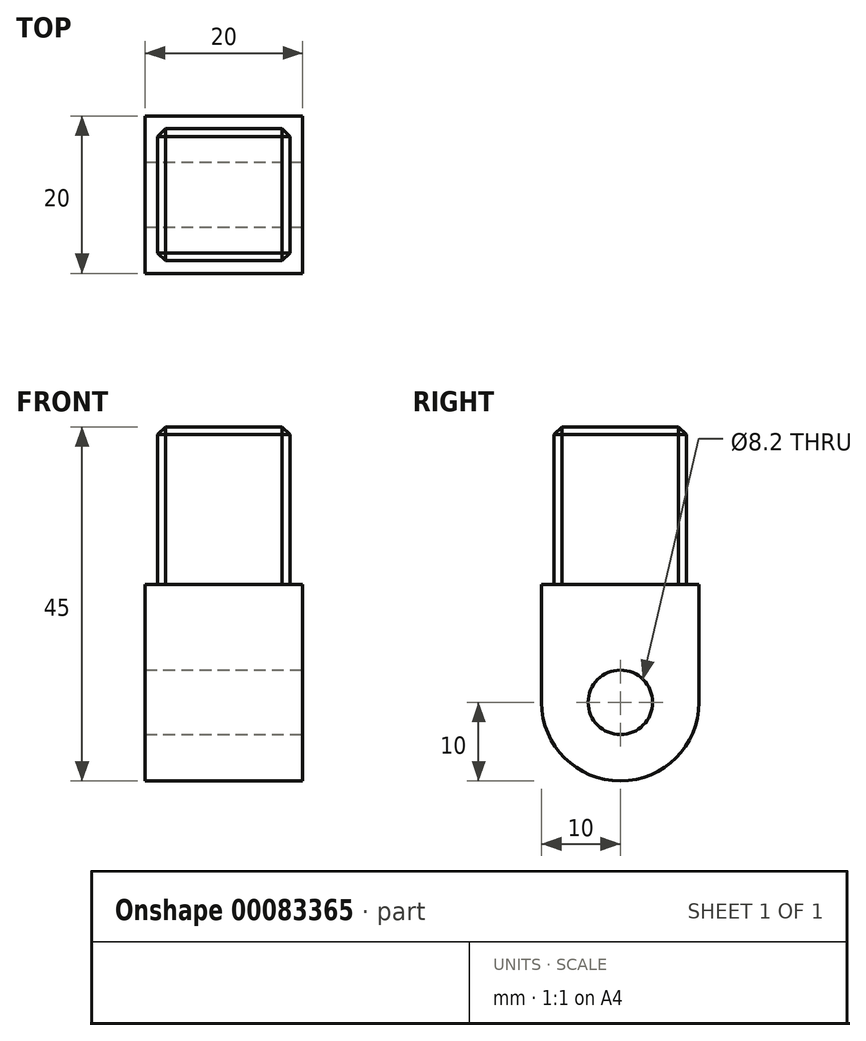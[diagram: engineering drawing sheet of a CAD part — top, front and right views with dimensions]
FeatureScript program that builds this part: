
annotation { "Feature Type Name" : "Feature", "Feature Type Description" : "" }
export const myFeature = defineFeature(function(context is Context, id is Id, definition is map)
    precondition{}
    {
        {
            var Q0;
            Q0=qCreatedBy(makeId("Top.planeOp"),FACE);
            var sketch = newSketch(context, id + "F0", { "sketchPlane" : qUnion([Q0])});
            skLineSegment(sketch, "E0", {"start": v(5, 20) * mm, "end": v(5, 0) * mm});
            skLineSegment(sketch, "E1", {"start": v(25, 20) * mm, "end": v(25, 0) * mm});
            skLineSegment(sketch, "E2", {"start": v(5, 20) * mm, "end": v(25, 20) * mm});
            skLineSegment(sketch, "E3", {"start": v(25, 0) * mm, "end": v(5, 0) * mm});
            skSolve(sketch);
        }
        {
            var Q0;
            {var subQ1=sQuery(id+"F0.wireOp",EDGE,"E0");Q0=makeQuery(id+"F0.imprint","IMPRINT",FACE,{"disambiguationData":[TD([[makeQuery(id+"F0.imprint","IMPRINT",EDGE,{"derivedFrom":subQ1}),1.0]])]});}
            extrude(context, id + "F1", {"entities" : qUnion([Q0]), "depth" : 25 * mm});
        }
        {
            var Q0;
            Q0=makeQuery(id+"F1.opExtrude","CAP_FACE",FACE,{"disambiguationData":[OSD([sQuery(id+"F0.wireOp",EDGE,"cecbb5cf-455c-4329-a757-5271d48d16f4.bottom"),sQuery(id+"F0.wireOp",EDGE,"cecbb5cf-455c-4329-a757-5271d48d16f4.top"),sQuery(id+"F0.wireOp",EDGE,"E0"),sQuery(id+"F0.wireOp",EDGE,"E1")])],"isStart":false});
            var sketch = newSketch(context, id + "F2", { "sketchPlane" : qUnion([Q0])});
            skLineSegment(sketch, "E4.0", {"start": v(6.6, 18.4) * mm, "end": v(23.4, 18.4) * mm});
            skLineSegment(sketch, "E4.1", {"start": v(6.6, 18.4) * mm, "end": v(6.6, 1.6) * mm});
            skLineSegment(sketch, "E4.2", {"start": v(23.4, 1.6) * mm, "end": v(6.6, 1.6) * mm});
            skLineSegment(sketch, "E4.3", {"start": v(23.4, 18.4) * mm, "end": v(23.4, 1.6) * mm});
            skSolve(sketch);
        }
        {
            var Q0;
            Q0=makeQuery(id+"F2.imprint","IMPRINT",FACE,{"disambiguationData":[TD([[makeQuery(id+"F2.imprint","IMPRINT",EDGE,{"derivedFrom":sQuery(id+"F2.wireOp",EDGE,"E4.0")}),-1.0]])]});
            extrude(context, id + "F3", {"entities" : qUnion([Q0]), "operationType" : NewBodyOperationType.ADD, "depth" : 20 * mm});
        }
        {
            var Q0;
            Q0=makeQuery(id+"F3.opExtrude","SWEPT_EDGE",EDGE,{"disambiguationData":[OSD([sQuery(id+"F2.wireOp",EDGE,"E4.0"),sQuery(id+"F2.wireOp",EDGE,"E4.1")])]});
            var Q1;
            Q1=makeQuery(id+"F3.opExtrude","CAP_EDGE",EDGE,{"disambiguationData":[OSD([sQuery(id+"F2.wireOp",EDGE,"E4.1")])],"isStart":false});
            var Q2;
            Q2=makeQuery(id+"F3.opExtrude","CAP_EDGE",EDGE,{"disambiguationData":[OSD([sQuery(id+"F2.wireOp",EDGE,"E4.0")])],"isStart":false});
            var Q3;
            Q3=makeQuery(id+"F3.opExtrude","SWEPT_EDGE",EDGE,{"disambiguationData":[OSD([sQuery(id+"F2.wireOp",EDGE,"E4.0"),sQuery(id+"F2.wireOp",EDGE,"E4.3")])]});
            var Q4;
            Q4=makeQuery(id+"F3.opExtrude","CAP_EDGE",EDGE,{"disambiguationData":[OSD([sQuery(id+"F2.wireOp",EDGE,"E4.3")])],"isStart":false});
            var Q5;
            Q5=makeQuery(id+"F3.opExtrude","CAP_EDGE",EDGE,{"disambiguationData":[OSD([sQuery(id+"F2.wireOp",EDGE,"E4.2")])],"isStart":false});
            var Q6;
            Q6=makeQuery(id+"F3.opExtrude","SWEPT_EDGE",EDGE,{"disambiguationData":[OSD([sQuery(id+"F2.wireOp",EDGE,"E4.1"),sQuery(id+"F2.wireOp",EDGE,"E4.2")])]});
            var Q7;
            Q7=makeQuery(id+"F3.opExtrude","SWEPT_EDGE",EDGE,{"disambiguationData":[OSD([sQuery(id+"F2.wireOp",EDGE,"E4.2"),sQuery(id+"F2.wireOp",EDGE,"E4.3")])]});
            chamfer(context, id + "F4", {"entities" : qUnion([Q0, Q1, Q2, Q3, Q4, Q5, Q6, Q7]), "width" : 1 * mm, "tangentPropagation" : true});
        }
        {
            var Q0;
            Q0=makeQuery(id+"F1.opExtrude","CAP_EDGE",EDGE,{"disambiguationData":[OSD([sQuery(id+"F0.wireOp",EDGE,"E3")])],"isStart":true});
            var Q1;
            Q1=makeQuery(id+"F1.opExtrude","CAP_EDGE",EDGE,{"disambiguationData":[OSD([sQuery(id+"F0.wireOp",EDGE,"E2")])],"isStart":true});
            fillet(context, id + "F5", {"entities" : qUnion([Q0, Q1]), "radius" : 10 * mm, "tangentPropagation" : true, "allowEdgeOverflow" : false});
        }
        {
            var Q0;
            Q0=makeQuery(id+"F1.opExtrude","SWEPT_FACE",FACE,{"disambiguationData":[OSD([sQuery(id+"F0.wireOp",EDGE,"E1")])]});
            var sketch = newSketch(context, id + "F6", { "sketchPlane" : qUnion([Q0])});
            skLineSegment(sketch, "E5", {"start": v(0, 10) * mm, "end": v(20, 10) * mm, "construction": true});
            skPoint(sketch, "E6", {"position": v(10, 10) * mm});
            skSolve(sketch);
        }
        {
            var Q0;
            Q0=sQuery(id+"F6.wireOp",VERTEX,"E6");
            var Q1;
            Q1=makeQuery(id+"F1.opExtrude","SWEPT_BODY",BODY,{"disambiguationData":[OSD([sQuery(id+"F0.wireOp",EDGE,"E0"),sQuery(id+"F0.wireOp",EDGE,"E1"),sQuery(id+"F0.wireOp",EDGE,"E2"),sQuery(id+"F0.wireOp",EDGE,"E3")])]});
            hole(context, id + "F7", {"style" : HoleStyle.SIMPLE, "endStyle" : HoleEndStyle.BLIND, "holeDiameter" : 8.2 * mm, "holeDepth" : 35 * mm, "locations" : qUnion([Q0]), "scope" : qUnion([Q1])});
        }
    });
